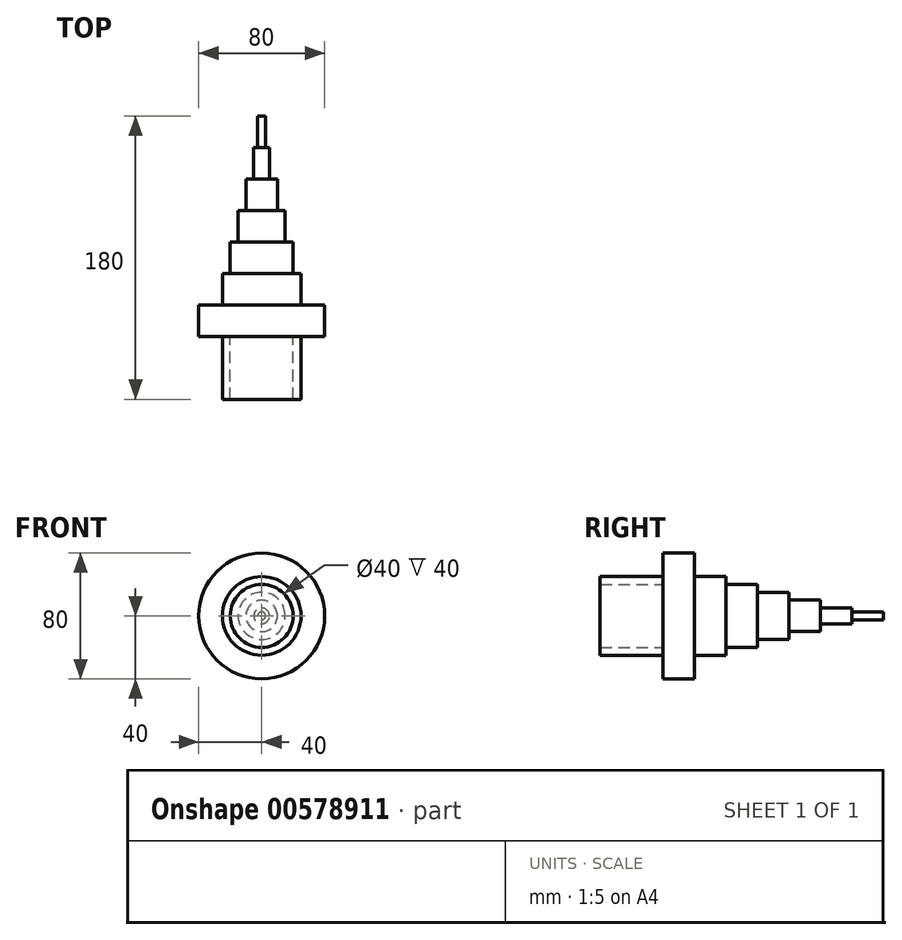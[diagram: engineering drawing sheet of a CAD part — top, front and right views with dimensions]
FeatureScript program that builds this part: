
annotation { "Feature Type Name" : "Feature", "Feature Type Description" : "" }
export const myFeature = defineFeature(function(context is Context, id is Id, definition is map)
    precondition{}
    {
        {
            var Q0;
            Q0=qCreatedBy(makeId("Front.planeOp"),FACE);
            var sketch = newSketch(context, id + "F0", { "sketchPlane" : qUnion([Q0])});
            skCircle(sketch, "E0", {"center": v(0, 0) * mm, "radius": 40 * mm});
            skSolve(sketch);
        }
        {
            var Q0;
            Q0 = qSketchRegion(id + "F0", true);
            extrude(context, id + "F1", {"entities" : qUnion([Q0]), "depth" : (180 - (20 * 6) - 40) * mm, "offsetDistance" : 25 * mm});
        }
        {
            var Q0;
            Q0=makeQuery(id+"F1.opExtrude","CAP_FACE",FACE,{"disambiguationData":[OSD([sQuery(id+"F0.wireOp",EDGE,"E0")])],"isStart":false});
            var sketch = newSketch(context, id + "F2", { "sketchPlane" : qUnion([Q0])});
            skCircle(sketch, "E1", {"center": v(0, 0) * mm, "radius": 25 * mm});
            skCircle(sketch, "E2", {"center": v(0, 0) * mm, "radius": 20 * mm});
            skSolve(sketch);
        }
        {
            var Q0;
            Q0=makeQuery(id+"F2.imprint","IMPRINT",FACE,{"disambiguationData":[TD([[makeQuery(id+"F2.imprint","IMPRINT",EDGE,{"derivedFrom":sQuery(id+"F2.wireOp",EDGE,"E1")}),1.0]])]});
            extrude(context, id + "F3", {"entities" : qUnion([Q0]), "operationType" : NewBodyOperationType.ADD, "depth" : 40 * mm, "offsetDistance" : 25 * mm});
        }
        {
            var Q0;
            Q0=makeQuery(id+"F1.opExtrude","CAP_FACE",FACE,{"disambiguationData":[OSD([sQuery(id+"F0.wireOp",EDGE,"E0")])],"isStart":true});
            var sketch = newSketch(context, id + "F4", { "sketchPlane" : qUnion([Q0])});
            skCircle(sketch, "E3", {"center": v(0, 0) * mm, "radius": 25 * mm});
            skSolve(sketch);
        }
        {
            var Q0;
            Q0 = qSketchRegion(id + "F4", true);
            extrude(context, id + "F5", {"entities" : qUnion([Q0]), "operationType" : NewBodyOperationType.ADD, "depth" : 20 * mm, "offsetDistance" : 25 * mm});
        }
        {
            var Q0;
            Q0=makeQuery(id+"F5.opExtrude","CAP_FACE",FACE,{"disambiguationData":[OSD([sQuery(id+"F4.wireOp",EDGE,"E3")])],"isStart":false});
            var sketch = newSketch(context, id + "F6", { "sketchPlane" : qUnion([Q0])});
            skCircle(sketch, "E4", {"center": v(0, 0) * mm, "radius": 20 * mm});
            skSolve(sketch);
        }
        {
            var Q0;
            Q0 = qSketchRegion(id + "F6", true);
            extrude(context, id + "F7", {"entities" : qUnion([Q0]), "operationType" : NewBodyOperationType.ADD, "depth" : 20 * mm, "offsetDistance" : 25 * mm});
        }
        {
            var Q0;
            Q0=makeQuery(id+"F7.opExtrude","CAP_FACE",FACE,{"disambiguationData":[OSD([sQuery(id+"F6.wireOp",EDGE,"E4")])],"isStart":false});
            var sketch = newSketch(context, id + "F8", { "sketchPlane" : qUnion([Q0])});
            skCircle(sketch, "E5", {"center": v(0, 0) * mm, "radius": 15 * mm});
            skSolve(sketch);
        }
        {
            var Q0;
            Q0 = qSketchRegion(id + "F8", true);
            extrude(context, id + "F9", {"entities" : qUnion([Q0]), "operationType" : NewBodyOperationType.ADD, "depth" : 20 * mm, "offsetDistance" : 25 * mm});
        }
        {
            var Q0;
            Q0=makeQuery(id+"F9.opExtrude","CAP_FACE",FACE,{"disambiguationData":[OSD([sQuery(id+"F8.wireOp",EDGE,"E5")])],"isStart":false});
            var sketch = newSketch(context, id + "F10", { "sketchPlane" : qUnion([Q0])});
            skCircle(sketch, "E6", {"center": v(0, 0) * mm, "radius": 10 * mm});
            skSolve(sketch);
        }
        {
            var Q0;
            Q0 = qSketchRegion(id + "F10", true);
            extrude(context, id + "F11", {"entities" : qUnion([Q0]), "operationType" : NewBodyOperationType.ADD, "depth" : 20 * mm, "offsetDistance" : 25 * mm});
        }
        {
            var Q0;
            Q0=makeQuery(id+"F11.opExtrude","CAP_FACE",FACE,{"disambiguationData":[OSD([sQuery(id+"F10.wireOp",EDGE,"E6")])],"isStart":false});
            var sketch = newSketch(context, id + "F12", { "sketchPlane" : qUnion([Q0])});
            skCircle(sketch, "E7", {"center": v(0, 0) * mm, "radius": 5 * mm});
            skSolve(sketch);
        }
        {
            var Q0;
            Q0 = qSketchRegion(id + "F12", true);
            extrude(context, id + "F13", {"entities" : qUnion([Q0]), "operationType" : NewBodyOperationType.ADD, "depth" : 20 * mm, "offsetDistance" : 25 * mm});
        }
        {
            var Q0;
            Q0=makeQuery(id+"F13.opExtrude","CAP_FACE",FACE,{"disambiguationData":[OSD([sQuery(id+"F12.wireOp",EDGE,"E7")])],"isStart":false});
            var sketch = newSketch(context, id + "F14", { "sketchPlane" : qUnion([Q0])});
            skCircle(sketch, "E8", {"center": v(0, 0) * mm, "radius": 2.5 * mm});
            skSolve(sketch);
        }
        {
            var Q0;
            Q0 = qSketchRegion(id + "F14", true);
            extrude(context, id + "F15", {"entities" : qUnion([Q0]), "operationType" : NewBodyOperationType.ADD, "depth" : 20 * mm, "offsetDistance" : 25 * mm});
        }
    });
